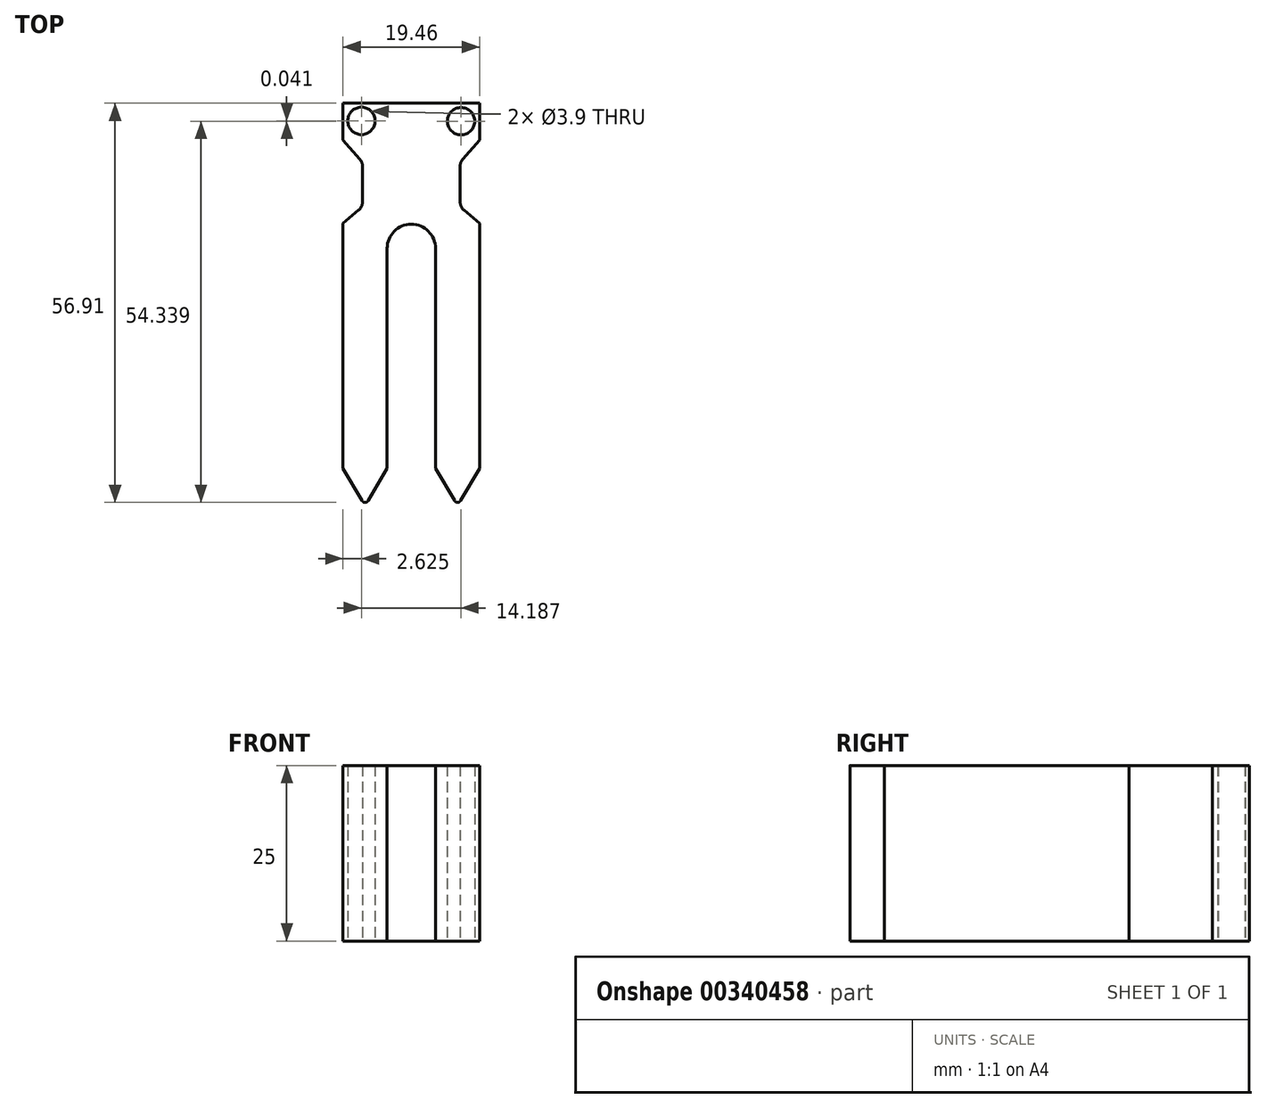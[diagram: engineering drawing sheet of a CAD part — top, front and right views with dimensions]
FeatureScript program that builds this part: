
annotation { "Feature Type Name" : "Feature", "Feature Type Description" : "" }
export const myFeature = defineFeature(function(context is Context, id is Id, definition is map)
    precondition{}
    {
        {
            var Q0;
            Q0=qCreatedBy(makeId("Top.planeOp"),FACE);
            var sketch = newSketch(context, id + "F0", { "sketchPlane" : qUnion([Q0])});
            skLineSegment(sketch, "E0", {"start": v(0, 0) * mm, "end": v(9.72, 0) * mm});
            skLineSegment(sketch, "E1", {"start": v(9.72, 0) * mm, "end": v(9.72, -5.28) * mm});
            skLineSegment(sketch, "E2", {"start": v(9.73, -5.28) * mm, "end": v(6.97, -8.42) * mm});
            skLineSegment(sketch, "E3", {"start": v(6.97, -8.42) * mm, "end": v(6.97, -14.8) * mm});
            skLineSegment(sketch, "E4", {"start": v(6.97, -14.8) * mm, "end": v(9.73, -17.13) * mm});
            skLineSegment(sketch, "E5", {"start": v(9.72, -17.13) * mm, "end": v(9.73, -52.04) * mm});
            skLineSegment(sketch, "E6", {"start": v(9.73, -52.04) * mm, "end": v(6.59, -57.4) * mm});
            skLineSegment(sketch, "E7", {"start": v(6.59, -57.4) * mm, "end": v(3.45, -52.04) * mm});
            skLineSegment(sketch, "E8", {"start": v(3.45, -52.04) * mm, "end": v(3.45, -20.7) * mm});
            skLineSegment(sketch, "E9.MirrorCS", {"start": v(0, 0) * mm, "end": v(-9.72, 0) * mm});
            skLineSegment(sketch, "E10.MirrorCS", {"start": v(-9.72, 0) * mm, "end": v(-9.72, -5.28) * mm});
            skLineSegment(sketch, "E11.MirrorCS", {"start": v(-9.72, -5.28) * mm, "end": v(-6.96, -8.42) * mm});
            skLineSegment(sketch, "E12.MirrorCS", {"start": v(-6.96, -8.42) * mm, "end": v(-6.96, -14.8) * mm});
            skLineSegment(sketch, "E13.MirrorCS", {"start": v(-6.96, -14.8) * mm, "end": v(-9.72, -17.13) * mm});
            skLineSegment(sketch, "E14.MirrorCS", {"start": v(-9.72, -17.13) * mm, "end": v(-9.72, -52.04) * mm});
            skLineSegment(sketch, "E15.MirrorCS", {"start": v(-3.44, -52.04) * mm, "end": v(-3.44, -20.7) * mm});
            skLineSegment(sketch, "E16.MirrorCS", {"start": v(-6.58, -57.4) * mm, "end": v(-3.44, -52.04) * mm});
            skLineSegment(sketch, "E17.MirrorCS", {"start": v(-9.72, -52.04) * mm, "end": v(-6.58, -57.4) * mm});
            skArc(sketch, "E18", {"start": v(3.45, -20.7) * mm, "mid": v(0, -17.26) * mm, "end": v(-3.44, -20.7) * mm});
            skCircle(sketch, "E19", {"center": v(-7.1, -2.53) * mm, "radius": 1.95 * mm});
            skCircle(sketch, "E20", {"center": v(7.08, -2.57) * mm, "radius": 1.95 * mm});
            skSolve(sketch);
        }
        {
            var Q0;
            Q0 = qSketchRegion(id + "F0", true);
            extrude(context, id + "F1", {"entities" : qUnion([Q0]), "depth" : 25 * mm});
        }
        {
            var Q0;
            Q0=makeQuery(id+"F1.opExtrude","SWEPT_EDGE",EDGE,{"disambiguationData":[OSD([sQuery(id+"F0.wireOp",EDGE,"E2"),sQuery(id+"F0.wireOp",EDGE,"E3")])]});
            var Q1;
            Q1=makeQuery(id+"F1.opExtrude","SWEPT_EDGE",EDGE,{"disambiguationData":[OSD([sQuery(id+"F0.wireOp",EDGE,"E3"),sQuery(id+"F0.wireOp",EDGE,"E4")])]});
            var Q2;
            Q2=makeQuery(id+"F1.opExtrude","SWEPT_EDGE",EDGE,{"disambiguationData":[OSD([sQuery(id+"F0.wireOp",EDGE,"E11.MirrorCS"),sQuery(id+"F0.wireOp",EDGE,"E12.MirrorCS")])]});
            var Q3;
            Q3=makeQuery(id+"F1.opExtrude","SWEPT_EDGE",EDGE,{"disambiguationData":[OSD([sQuery(id+"F0.wireOp",EDGE,"E12.MirrorCS"),sQuery(id+"F0.wireOp",EDGE,"E13.MirrorCS")])]});
            fillet(context, id + "F2", {"entities" : qUnion([Q0, Q1, Q2, Q3]), "radius" : 1.5 * mm, "tangentPropagation" : true, "allowEdgeOverflow" : false});
        }
        {
            var Q0;
            Q0=makeQuery(id+"F1.opExtrude","SWEPT_EDGE",EDGE,{"disambiguationData":[OSD([sQuery(id+"F0.wireOp",EDGE,"E16.MirrorCS"),sQuery(id+"F0.wireOp",EDGE,"E17.MirrorCS")])]});
            var Q1;
            Q1=makeQuery(id+"F1.opExtrude","SWEPT_EDGE",EDGE,{"disambiguationData":[OSD([sQuery(id+"F0.wireOp",EDGE,"E6"),sQuery(id+"F0.wireOp",EDGE,"E7")])]});
            fillet(context, id + "F3", {"entities" : qUnion([Q0, Q1]), "radius" : .5 * mm, "tangentPropagation" : true, "allowEdgeOverflow" : false});
        }
    });
